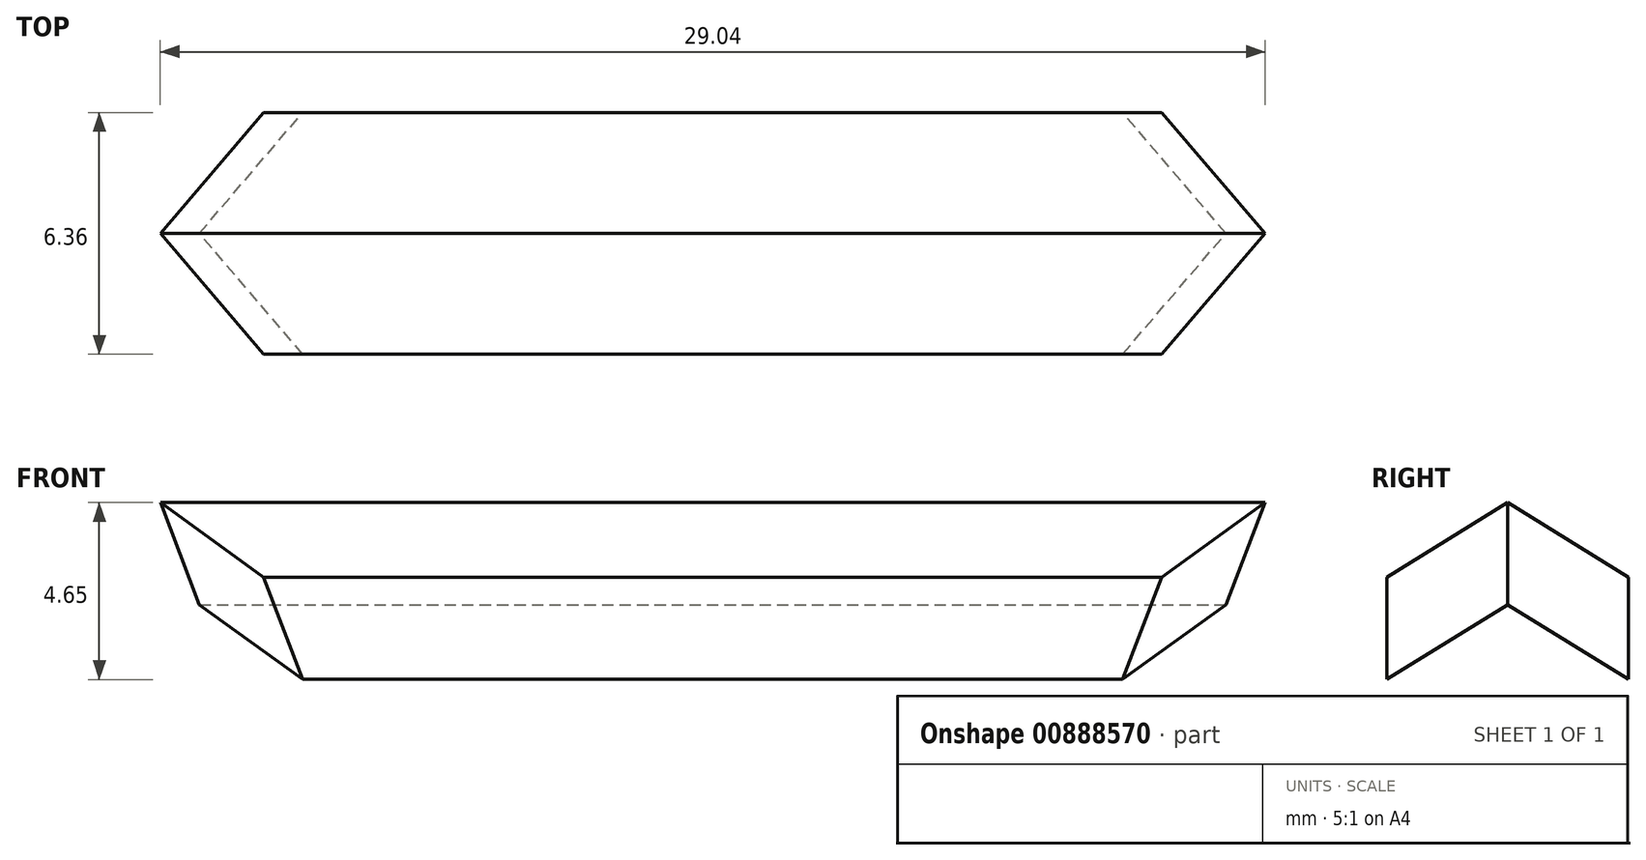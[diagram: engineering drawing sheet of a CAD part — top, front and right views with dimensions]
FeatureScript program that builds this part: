
annotation { "Feature Type Name" : "Feature", "Feature Type Description" : "" }
export const myFeature = defineFeature(function(context is Context, id is Id, definition is map)
    precondition{}
    {
        {
            var Q0;
            Q0=qCreatedBy(makeId("Right.planeOp"),FACE);
            var sketch = newSketch(context, id + "F0", { "sketchPlane" : qUnion([Q0])});
            skLineSegment(sketch, "E0.bottom", {"start": v(15.87, 19.05) * mm, "end": v(-15.88, 19.05) * mm});
            skLineSegment(sketch, "E0.top", {"start": v(15.87, -19.05) * mm, "end": v(-15.88, -19.05) * mm});
            skLineSegment(sketch, "E0.left", {"start": v(15.88, 19.05) * mm, "end": v(15.88, -19.05) * mm});
            skLineSegment(sketch, "E0.right", {"start": v(-15.88, 19.05) * mm, "end": v(-15.88, -19.05) * mm});
            skPoint(sketch, "E0.middle", {"position": v(0, 0) * mm});
            skSolve(sketch);
        }
        {
            var Q0;
            Q0 = qSketchRegion(id + "F0", true);
            extrude(context, id + "F1", {"entities" : qUnion([Q0]), "depth" : 19.05 * mm, "offsetDistance" : 25.4 * mm});
        }
        {
            var Q0;
            Q0=makeQuery(id+"F1.opExtrude","CAP_FACE",FACE,{"disambiguationData":[OSD([sQuery(id+"F0.wireOp",EDGE,"E0.bottom"),sQuery(id+"F0.wireOp",EDGE,"E0.top"),sQuery(id+"F0.wireOp",EDGE,"E0.left"),sQuery(id+"F0.wireOp",EDGE,"E0.right")])],"isStart":false});
            var sketch = newSketch(context, id + "F2", { "sketchPlane" : qUnion([Q0])});
            skLineSegment(sketch, "E1", {"start": v(0, 19.05) * mm, "end": v(15.88, 9.25) * mm});
            skLineSegment(sketch, "E2", {"start": v(15.88, 9.25) * mm, "end": v(15.88, 19.05) * mm});
            skLineSegment(sketch, "E3", {"start": v(15.87, 19.05) * mm, "end": v(0, 19.05) * mm});
            skLineSegment(sketch, "E4", {"start": v(0, 19.05) * mm, "end": v(-15.88, 9.25) * mm});
            skLineSegment(sketch, "E5", {"start": v(-15.88, 9.25) * mm, "end": v(-15.88, 19.05) * mm});
            skLineSegment(sketch, "E6", {"start": v(-15.88, 19.05) * mm, "end": v(0, 19.05) * mm});
            skLineSegment(sketch, "E7", {"start": v(15.88, -19.05) * mm, "end": v(-15.88, -19.05) * mm});
            skLineSegment(sketch, "E8", {"start": v(-15.88, -19.05) * mm, "end": v(-15.88, 6.56) * mm});
            skLineSegment(sketch, "E9", {"start": v(-15.88, 6.56) * mm, "end": v(0, 16.36) * mm});
            skLineSegment(sketch, "E10", {"start": v(0, 16.36) * mm, "end": v(15.88, 6.56) * mm});
            skLineSegment(sketch, "E11", {"start": v(15.88, 6.56) * mm, "end": v(15.88, -19.05) * mm});
            skSolve(sketch);
        }
        {
            var Q0;
            Q0 = qSketchRegion(id + "F2", true);
            extrude(context, id + "F3", {"entities" : qUnion([Q0]), "operationType" : NewBodyOperationType.REMOVE, "endBound" : BoundingType.THROUGH_ALL, "oppositeDirection" : true, "depth" : 25.4 * mm, "offsetDistance" : 25.4 * mm});
        }
        {
            var Q0;
            Q0=makeQuery(id+"F3.boolean.opBoolean","COPY",FACE,{"derivedFrom":makeQuery(id+"F3.opExtrude","SWEPT_FACE",FACE,{"disambiguationData":[OSD([sQuery(id+"F2.wireOp",EDGE,"E4")])]})});
            var sketch = newSketch(context, id + "F4", { "sketchPlane" : qUnion([Q0])});
            skLineSegment(sketch, "E12", {"start": v(19.05, 16.25) * mm, "end": v(-0.07, -10.06) * mm});
            skLineSegment(sketch, "E13", {"start": v(-0.07, -10.06) * mm, "end": v(19.05, -10.06) * mm});
            skLineSegment(sketch, "E14", {"start": v(19.05, -10.06) * mm, "end": v(19.05, 16.25) * mm});
            skSolve(sketch);
        }
        {
            var Q0;
            Q0 = qSketchRegion(id + "F4", true);
            extrude(context, id + "F5", {"entities" : qUnion([Q0]), "operationType" : NewBodyOperationType.REMOVE, "endBound" : BoundingType.THROUGH_ALL, "oppositeDirection" : true, "depth" : 25.4 * mm, "offsetDistance" : 25.4 * mm});
        }
        {
            var Q0;
            Q0=makeQuery(id+"F3.boolean.opBoolean","COPY",FACE,{"derivedFrom":makeQuery(id+"F3.opExtrude","SWEPT_FACE",FACE,{"disambiguationData":[OSD([sQuery(id+"F2.wireOp",EDGE,"E1")])]})});
            var sketch = newSketch(context, id + "F6", { "sketchPlane" : qUnion([Q0])});
            skLineSegment(sketch, "E15", {"start": v(125.31, 10.06) * mm, "end": v(125.31, -10.01) * mm});
            skLineSegment(sketch, "E16", {"start": v(125.31, -10.01) * mm, "end": v(110.73, 10.06) * mm});
            skLineSegment(sketch, "E17", {"start": v(110.73, 10.06) * mm, "end": v(125.31, 10.06) * mm});
            skSolve(sketch);
        }
        {
            var Q0;
            Q0 = qSketchRegion(id + "F6", true);
            extrude(context, id + "F7", {"entities" : qUnion([Q0]), "operationType" : NewBodyOperationType.REMOVE, "endBound" : BoundingType.THROUGH_ALL, "oppositeDirection" : true, "depth" : 25.4 * mm, "offsetDistance" : 25.4 * mm});
        }
        {
            var Q0;
            Q0=makeQuery(id+"F3.boolean.opBoolean","COPY",FACE,{"derivedFrom":makeQuery(id+"F3.opExtrude","SWEPT_FACE",FACE,{"disambiguationData":[OSD([sQuery(id+"F2.wireOp",EDGE,"E1")])]})});
            var sketch = newSketch(context, id + "F8", { "sketchPlane" : qUnion([Q0])});
            skLineSegment(sketch, "E18", {"start": v(19.05, -16.25) * mm, "end": v(19.05, 10.06) * mm});
            skLineSegment(sketch, "E19", {"start": v(19.05, 10.06) * mm, "end": v(-0.07, 10.06) * mm});
            skLineSegment(sketch, "E20", {"start": v(-0.07, 10.06) * mm, "end": v(19.05, -16.25) * mm});
            skSolve(sketch);
        }
        {
            var Q0;
            Q0 = qSketchRegion(id + "F8", true);
            extrude(context, id + "F9", {"entities" : qUnion([Q0]), "operationType" : NewBodyOperationType.REMOVE, "oppositeDirection" : true, "depth" : 25.4 * mm, "offsetDistance" : 25.4 * mm});
        }
        {
            var Q0;
            Q0=makeQuery(id+"F1.opExtrude","SWEPT_BODY",BODY,{"disambiguationData":[OSD([sQuery(id+"F0.wireOp",EDGE,"E0.bottom"),sQuery(id+"F0.wireOp",EDGE,"E0.top"),sQuery(id+"F0.wireOp",EDGE,"E0.left"),sQuery(id+"F0.wireOp",EDGE,"E0.right")])]});
            var Q1;
            Q1=qCreatedBy(makeId("Right.planeOp"),FACE);
            mirror(context, id + "F10", {"operationType" : NewBodyOperationType.ADD, "entities" : qUnion([Q0]), "mirrorPlane" : qUnion([Q1])});
        }
        {
            var Q0;
            Q0=qCreatedBy(makeId("Right.planeOp"),FACE);
            var sketch = newSketch(context, id + "F11", { "sketchPlane" : qUnion([Q0])});
            skLineSegment(sketch, "E21", {"start": v(-15.87, 6.56) * mm, "end": v(-15.87, 9.25) * mm});
            skLineSegment(sketch, "E22", {"start": v(-15.87, 9.25) * mm, "end": v(-3.18, 17.09) * mm});
            skLineSegment(sketch, "E23", {"start": v(-3.18, 17.09) * mm, "end": v(-3.17, 14.4) * mm});
            skLineSegment(sketch, "E24", {"start": v(-3.17, 14.4) * mm, "end": v(-15.88, 6.56) * mm});
            skLineSegment(sketch, "E25", {"start": v(3.18, 17.09) * mm, "end": v(15.88, 9.25) * mm});
            skLineSegment(sketch, "E26", {"start": v(15.88, 9.25) * mm, "end": v(15.88, 6.56) * mm});
            skLineSegment(sketch, "E27", {"start": v(15.88, 6.56) * mm, "end": v(3.17, 14.4) * mm});
            skLineSegment(sketch, "E28", {"start": v(3.18, 14.4) * mm, "end": v(3.18, 17.09) * mm});
            skSolve(sketch);
        }
        {
            var Q0;
            Q0 = qSketchRegion(id + "F11", true);
            extrude(context, id + "F12", {"entities" : qUnion([Q0]), "operationType" : NewBodyOperationType.REMOVE, "endBound" : BoundingType.THROUGH_ALL, "oppositeDirection" : true, "depth" : 25.4 * mm, "offsetDistance" : 25.4 * mm, "hasSecondDirection" : true, "secondDirectionBound" : SecondDirectionBoundingType.THROUGH_ALL, "secondDirectionOppositeDirection" : false, "secondDirectionDepth" : 25.4 * mm});
        }
    });
